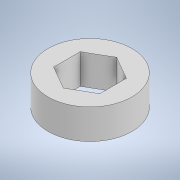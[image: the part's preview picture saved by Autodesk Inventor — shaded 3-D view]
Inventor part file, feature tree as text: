
AUTODESK INVENTOR PART (.ipt)
format: ipt  version: 2022.2 (Build 262287010, 287A)  size: 106,496 bytes
history: native  units: in
note: dims shown in document units (in); Inventor stores cm internally (conversion verified against a paired STEP export)
features: extrude x1, sketch x1
ambient origin geometry x8: Origin, YZ Plane, XZ Plane, XY Plane, X Axis, Y Axis, Z Axis, Center Point
bodies: Solid1 (feature_tree)
feature tree (2):
  extrude  "Extrusion1"  Depth=0.25in
  sketch  "Sketch1"  dims[d0=0.385in d1=0.7in d2=0.25in d3=0.0in]
